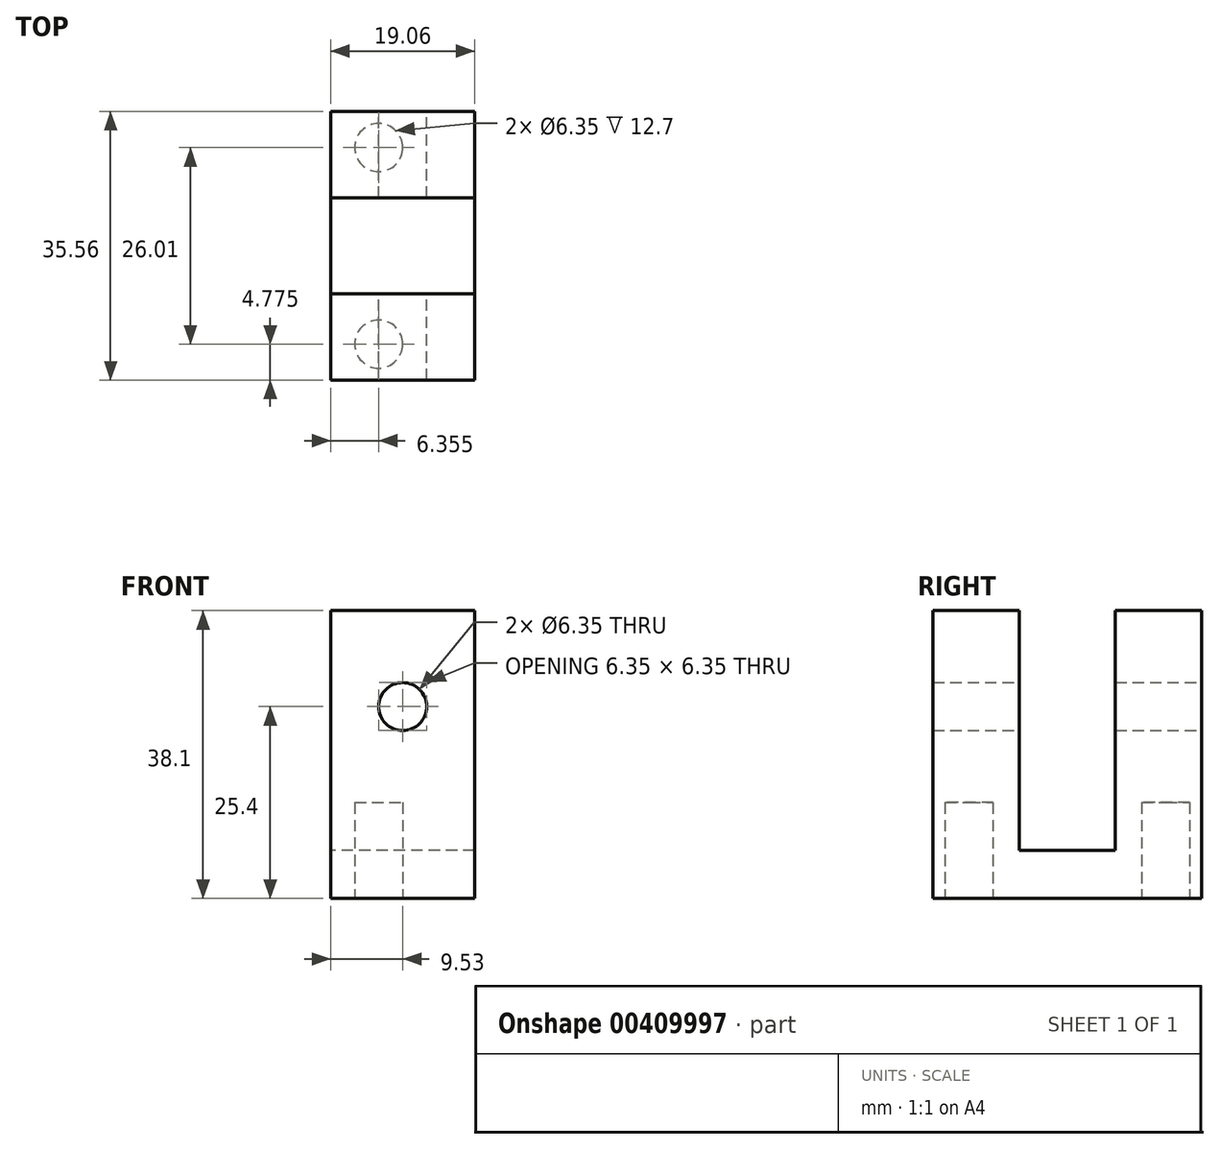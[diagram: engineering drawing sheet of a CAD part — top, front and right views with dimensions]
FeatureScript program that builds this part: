
annotation { "Feature Type Name" : "Feature", "Feature Type Description" : "" }
export const myFeature = defineFeature(function(context is Context, id is Id, definition is map)
    precondition{}
    {
        {
            var Q0;
            Q0=qCreatedBy(makeId("Front.planeOp"),FACE);
            var sketch = newSketch(context, id + "F0", { "sketchPlane" : qUnion([Q0])});
            skCircle(sketch, "E0", {"center": v(0, 0) * mm, "radius": 3.18 * mm});
            skLineSegment(sketch, "E1.bottom", {"start": v(-9.53, 12.7) * mm, "end": v(9.53, 12.7) * mm});
            skLineSegment(sketch, "E1.top", {"start": v(-9.52, -25.4) * mm, "end": v(9.52, -25.4) * mm});
            skLineSegment(sketch, "E1.left", {"start": v(-9.53, 12.7) * mm, "end": v(-9.52, -25.4) * mm});
            skLineSegment(sketch, "E1.right", {"start": v(9.53, 12.7) * mm, "end": v(9.52, -25.4) * mm});
            skSolve(sketch);
        }
        {
            var Q0;
            Q0 = qSketchRegion(id + "F0", true);
            extrude(context, id + "F1", {"entities" : qUnion([Q0]), "depth" : 35.56 * mm});
        }
        {
            var Q0;
            Q0=makeQuery(id+"F1.opExtrude","SWEPT_FACE",FACE,{"disambiguationData":[OSD([sQuery(id+"F0.wireOp",EDGE,"E1.left")])]});
            var sketch = newSketch(context, id + "F2", { "sketchPlane" : qUnion([Q0])});
            skLineSegment(sketch, "E2.bottom", {"start": v(11.43, 12.7) * mm, "end": v(24.13, 12.7) * mm});
            skLineSegment(sketch, "E2.top", {"start": v(11.43, -19.05) * mm, "end": v(24.13, -19.05) * mm});
            skLineSegment(sketch, "E2.left", {"start": v(11.43, 12.7) * mm, "end": v(11.43, -19.05) * mm});
            skLineSegment(sketch, "E2.right", {"start": v(24.13, 12.7) * mm, "end": v(24.13, -19.05) * mm});
            skLineSegment(sketch, "E3", {"start": v(17.78, 32.3) * mm, "end": v(17.78, -40.22) * mm, "construction": true});
            skLineSegment(sketch, "E4", {"start": v(-12.35, 0) * mm, "end": v(61.08, 0) * mm, "construction": true});
            skSolve(sketch);
        }
        {
            var Q0;
            Q0 = qSketchRegion(id + "F2", true);
            extrude(context, id + "F3", {"entities" : qUnion([Q0]), "operationType" : NewBodyOperationType.REMOVE, "endBound" : BoundingType.THROUGH_ALL, "oppositeDirection" : true, "depth" : 25.4 * mm});
        }
        {
            var Q0;
            Q0=makeQuery(id+"F1.opExtrude","SWEPT_FACE",FACE,{"disambiguationData":[OSD([sQuery(id+"F0.wireOp",EDGE,"E1.top")])]});
            var sketch = newSketch(context, id + "F4", { "sketchPlane" : qUnion([Q0])});
            skLineSegment(sketch, "E5", {"start": v(0, -47.95) * mm, "end": v(0, 167.18) * mm, "construction": true});
            skLineSegment(sketch, "E6", {"start": v(-79.16, 17.78) * mm, "end": v(82.58, 17.78) * mm, "construction": true});
            skCircle(sketch, "E7", {"center": v(-3.17, 4.78) * mm, "radius": 3.17 * mm});
            skCircle(sketch, "E8.MirrorC", {"center": v(-3.17, 30.78) * mm, "radius": 3.17 * mm});
            skSolve(sketch);
        }
        {
            var Q0;
            Q0 = qSketchRegion(id + "F4", true);
            extrude(context, id + "F5", {"entities" : qUnion([Q0]), "operationType" : NewBodyOperationType.REMOVE, "oppositeDirection" : true, "depth" : 12.7 * mm});
        }
    });
